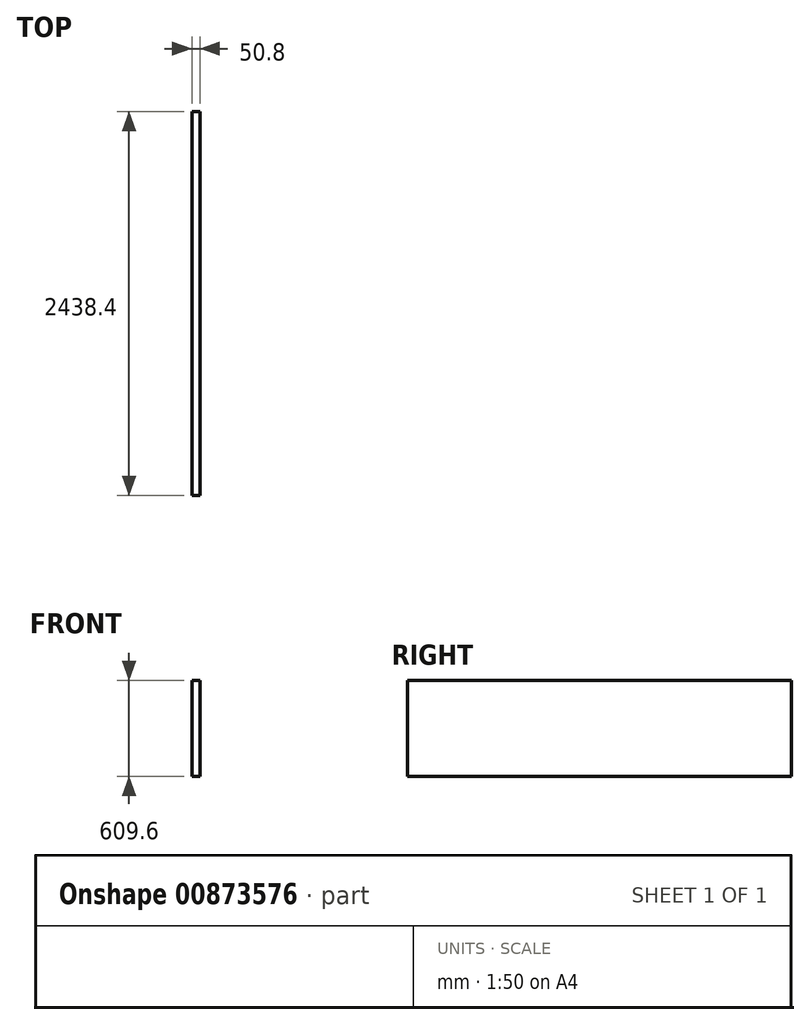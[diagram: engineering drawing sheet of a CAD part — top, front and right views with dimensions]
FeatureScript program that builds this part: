
annotation { "Feature Type Name" : "Feature", "Feature Type Description" : "" }
export const myFeature = defineFeature(function(context is Context, id is Id, definition is map)
    precondition{}
    {
        {
            var Q0;
            Q0=qCreatedBy(makeId("Top.planeOp"),FACE);
            var sketch = newSketch(context, id + "F0", { "sketchPlane" : qUnion([Q0])});
            skLineSegment(sketch, "E0.bottom", {"start": v(0, 0) * mm, "end": v(50.8, 0) * mm});
            skLineSegment(sketch, "E0.top", {"start": v(0, 2438.4) * mm, "end": v(50.8, 2438.4) * mm});
            skLineSegment(sketch, "E0.left", {"start": v(0, 0) * mm, "end": v(0, 2438.4) * mm});
            skLineSegment(sketch, "E0.right", {"start": v(50.8, 0) * mm, "end": v(50.8, 2438.4) * mm});
            skSolve(sketch);
        }
        {
            var Q0;
            Q0=makeQuery(id+"F0.imprint","IMPRINT",FACE,{"disambiguationData":[TD([[makeQuery(id+"F0.imprint","IMPRINT",EDGE,{"derivedFrom":sQuery(id+"F0.wireOp",EDGE,"E0.bottom")}),1.0]])]});
            extrude(context, id + "F1", {"entities" : qUnion([Q0]), "depth" : 609.6 * mm, "offsetDistance" : 25.4 * mm});
        }
    });
